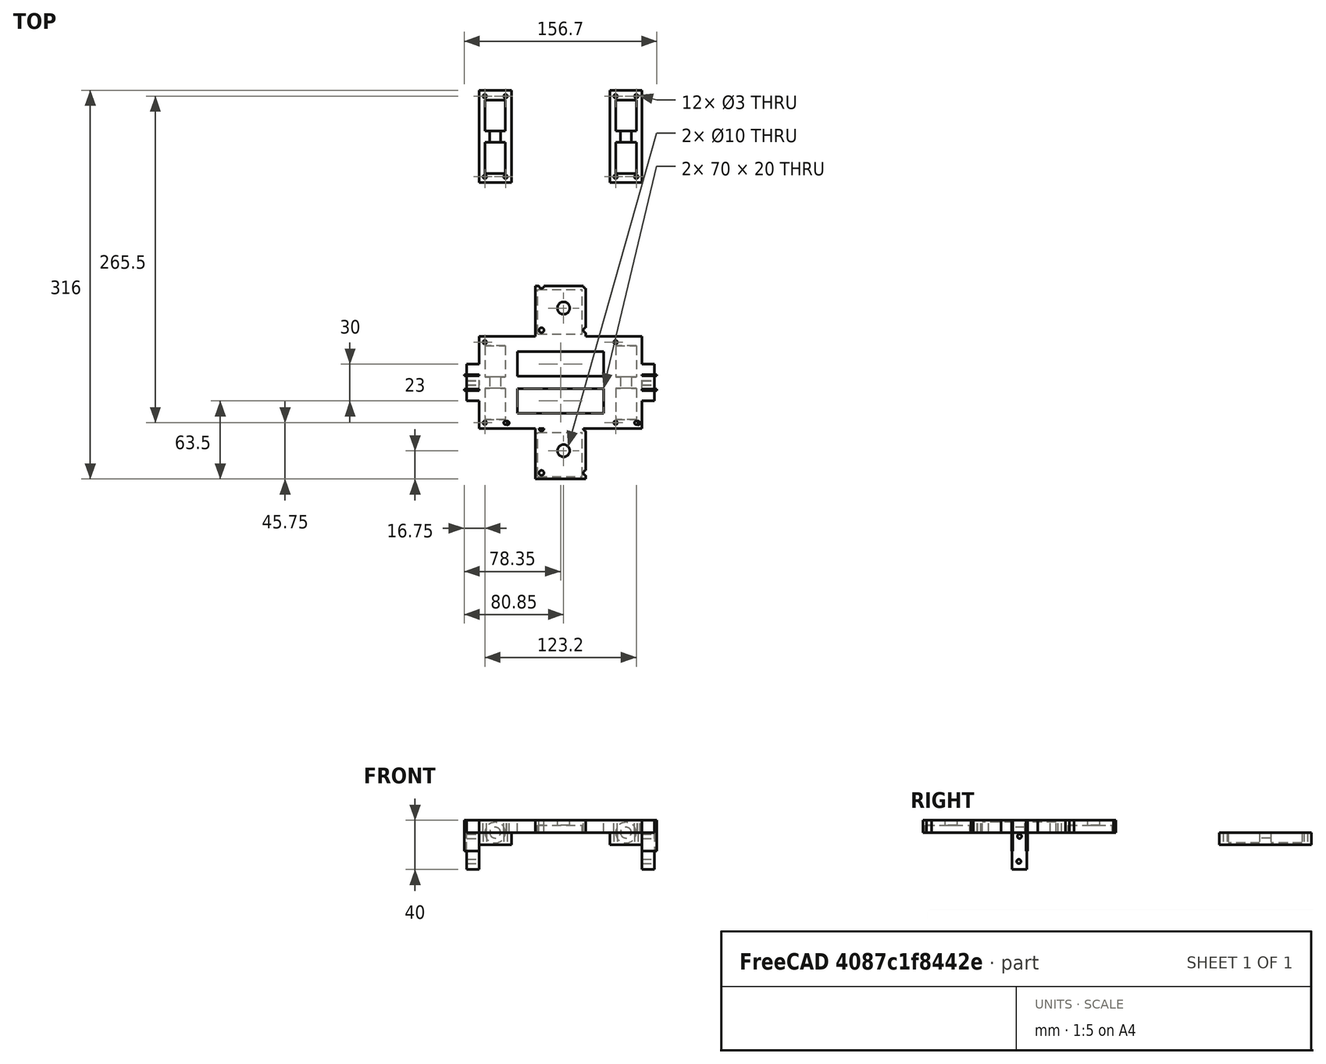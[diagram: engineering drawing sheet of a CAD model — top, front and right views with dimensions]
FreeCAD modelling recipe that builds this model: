
FCSTD DOCUMENT  (FreeCAD 0.16R6712 (Git))
Label: 1.2
License: All rights reserved
LicenseURL: http://en.wikipedia.org/wiki/All_rights_reserved
objects: Part::Cut×24, Part::Cylinder×21, Part::Box×14, Part::Fuse×5, Part::FeaturePython×4, Part::MultiFuse×4
note: 72 computed .brp shape members not serialized (recipe doc carries the construction recipe); baked Part::Feature solids carry a one-line shape summary decoded from their .brp

FEATURE [Part::Box] Box  label="Cubo"
  Height = 10
  Length = 26.35
  Width = 75
FEATURE [Part::Cylinder] Cylinder  label="Cilindro"
  Angle = 360
  Height = 10
  Placement = pos=(4.75,4.75,0) rot=(0,0,1;0rad)
  Radius = 1.5
FEATURE [Part::Cylinder] Cylinder002  label="Cilindro002"
  Angle = 360
  Height = 10
  Placement = pos=(4.75,70.25,0) rot=(0,0,1;0rad)
  Radius = 1.5
FEATURE [Part::Cylinder] Cylinder003  label="Cilindro003"
  Angle = 360
  Height = 10
  Placement = pos=(23.1425,4.56262,6.40077e-06) rot=(0,0,1;0rad)
  Radius = 1.5
FEATURE [Part::Cut] Cut
  Base = -> Box
  Tool = -> Cylinder
FEATURE [Part::Cut] Cut001
  Base = -> Cut
  Tool = -> Cylinder002
FEATURE [Part::Cut] Cut002
  Base = -> Cut001
  Tool = -> Cylinder003
FEATURE [Part::Cylinder] Cylinder004  label="Cilindro004"
  Angle = 360
  Height = 25.35
  Placement = pos=(13.175,30,0) rot=(1,0,0;1.5708rad)
  Radius = 8.4
FEATURE [Part::Cylinder] Cylinder005  label="Cilindro005"
  Angle = 360
  Height = 25.35
  Placement = pos=(13.175,64.5,0) rot=(1,0,0;1.5708rad)
  Radius = 8.4
FEATURE [Part::Cylinder] Cylinder006  label="Cilindro006"
  Angle = 360
  Height = 9.5
  Placement = pos=(13.175,39.5,0) rot=(1,0,0;1.5708rad)
  Radius = 4.4
FEATURE [Part::Fuse] Fusion
  Base = -> Cylinder004
  Tool = -> Cylinder005
FEATURE [Part::Fuse] Fusion001
  Base = -> Fusion
  Placement = pos=(0,2.75,0) rot=(0,0,1;0rad)
  Tool = -> Cylinder006
FEATURE [Part::Cylinder] Cylinder001  label="Cilindro001"
  Angle = 360
  Height = 10
  Placement = pos=(21.6,4.75,0) rot=(0,0,1;0rad)
  Radius = 1.5
FEATURE [Part::Cut] Cut004
  Base = -> Cut002
  Tool = -> Cylinder001
FEATURE [Part::Cut] Cut003
  Base = -> Cut002
  Tool = -> Cylinder001
FEATURE [Part::Fuse] Fusion002
  Base = -> Cut004
  Tool = -> Cut003
FEATURE [Part::Cut] Cut005
  Base = -> Fusion002
  Tool = -> Fusion001
FEATURE [Part::Cut] Cut006
  Base = -> Cut005
  Tool = -> Cylinder001
FEATURE [Part::FeaturePython] Array  label="Carrileras"  # Draft array (typed FeaturePython)
  Angle = 360
  ArrayType = 0
  Axis = (0,0,1)
  Base = -> Cut006
  Center = (0,0,0)
  Fuse = false
  IntervalAxis = (0,0,0)
  IntervalX = (106.35,0,0)
  IntervalY = (0,1,0)
  IntervalZ = (0,0,0)
  NumberPolar = 1
  NumberX = 2
  NumberY = 1
  NumberZ = 1
FEATURE [Part::Box] Box001  label="Centro"
  Height = 10
  Length = 80
  Placement = pos=(26.35,0,0) rot=(0,0,1;0rad)
  Width = 75
FEATURE [Part::Box] Box002  label="Lucernario"
  Height = 10
  Length = 70
  Placement = pos=(31.35,12.5,0) rot=(0,0,1;0rad)
  Width = 20
FEATURE [Part::Box] Box003  label="Lucernario2"
  Height = 10
  Length = 70
  Placement = pos=(31.35,42.5,0) rot=(0,0,1;0rad)
  Width = 20
FEATURE [Part::Cut] Cut007
  Base = -> Box001
  Tool = -> Box002
FEATURE [Part::Cut] Cut008  label="Centro1"
  Base = -> Cut007
  Tool = -> Box003
FEATURE [Part::Box] Box006  label="Guia1"
  Height = 10
  Length = 10
  Placement = pos=(-10,22.5,0) rot=(0,0,1;0rad)
  Width = 30
FEATURE [Part::Box] Box007  label="Guia2"
  Height = 10
  Length = 10
  Placement = pos=(132.7,22.5,0) rot=(0,0,1;0rad)
  Width = 30
FEATURE [Part::Fuse] Fusion005
  Base = -> Array
  Tool = -> Box006
FEATURE [Part::MultiFuse] Fusion006  label="Carrileras y guias"
  Shapes = -> [Fusion005,Box007]
FEATURE [Part::Box] Box010  label="Cubo003"
  Height = 10
  Length = 26.35
  Width = 75
FEATURE [Part::Cylinder] Cylinder007  label="Cilindro007"
  Angle = 360
  Height = 25.35
  Placement = pos=(13.175,67.25,0) rot=(1,0,0;1.5708rad)
  Radius = 8.4
FEATURE [Part::Cut] Cut011
  Base = -> Box010
  Tool = -> Cylinder007
FEATURE [Part::Cylinder] Cylinder008  label="Cilindro008"
  Angle = 360
  Height = 9.5
  Placement = pos=(13.175,42.25,0) rot=(1,0,0;1.5708rad)
  Radius = 4.4
FEATURE [Part::Cut] Cut012
  Base = -> Cut011
  Tool = -> Cylinder008
FEATURE [Part::Cylinder] Cylinder009  label="Cilindro009"
  Angle = 360
  Height = 25.35
  Placement = pos=(13.175,32.75,0) rot=(1,0,0;1.5708rad)
  Radius = 8.4
FEATURE [Part::Cut] Cut013
  Base = -> Cut012
  Tool = -> Cylinder009
FEATURE [Part::Cylinder] Cylinder010  label="Cilindro010"
  Angle = 360
  Height = 10
  Placement = pos=(21.6,4.75,0) rot=(0,0,1;0rad)
  Radius = 1.5
FEATURE [Part::Cylinder] Cylinder011  label="Cilindro011"
  Angle = 360
  Height = 10
  Placement = pos=(4.75,4.75,0) rot=(0,0,1;0rad)
  Radius = 1.5
FEATURE [Part::Cut] Cut014
  Base = -> Cut013
  Tool = -> Cylinder010
FEATURE [Part::Cut] Cut015
  Base = -> Cut014
  Tool = -> Cylinder011
FEATURE [Part::Cylinder] Cylinder012  label="Cilindro012"
  Angle = 360
  Height = 10
  Placement = pos=(4.75,70.25,0) rot=(0,0,1;0rad)
  Radius = 1.5
FEATURE [Part::Cylinder] Cylinder013  label="Cilindro013"
  Angle = 360
  Height = 10
  Placement = pos=(21.6,70.25,0) rot=(0,0,1;0rad)
  Radius = 1.5
FEATURE [Part::Cut] Cut016
  Base = -> Cut015
  Tool = -> Cylinder012
FEATURE [Part::Cut] Cut017
  Base = -> Cut016
  Placement = pos=(0,0,0) rot=(0,1,0;3.14159rad)
  Tool = -> Cylinder013
FEATURE [Part::FeaturePython] Array001  label="Cierres"  # Draft array (typed FeaturePython)
  Angle = 360
  ArrayType = 0
  Axis = (0,0,1)
  Base = -> Cut017
  Center = (0,0,0)
  Fuse = false
  IntervalAxis = (0,0,0)
  IntervalX = (106.35,0,0)
  IntervalY = (0,1,0)
  IntervalZ = (0,0,0)
  NumberPolar = 1
  NumberX = 2
  NumberY = 1
  NumberZ = 1
  Placement = pos=(26.35,200,0) rot=(0,0,1;0rad)
FEATURE [Part::Box] Box011  label="Cubo004"
  Height = 10
  Length = 41
  Width = 41
FEATURE [Part::Cylinder] Cylinder014  label="Cilindro014"
  Angle = 360
  Height = 10
  Placement = pos=(5,5,0) rot=(0,0,1;0rad)
  Radius = 2
FEATURE [Part::Cylinder] Cylinder015  label="Cilindro015"
  Angle = 360
  Height = 10
  Placement = pos=(5,41,0) rot=(0,0,1;0rad)
  Radius = 2
FEATURE [Part::Cylinder] Cylinder016  label="Cilindro016"
  Angle = 360
  Height = 10
  Placement = pos=(41,5,0) rot=(0,0,1;0rad)
  Radius = 2
FEATURE [Part::Cylinder] Cylinder017  label="Cilindro017"
  Angle = 360
  Height = 10
  Placement = pos=(41,41,0) rot=(0,0,1;0rad)
  Radius = 2
FEATURE [Part::Cylinder] Cylinder018  label="Cilindro018"
  Angle = 360
  Height = 10
  Placement = pos=(23,23,0) rot=(0,0,1;0rad)
  Radius = 5
FEATURE [Part::Cut] Cut018
  Base = -> Box011
  Tool = -> Cylinder015
FEATURE [Part::Cut] Cut019
  Base = -> Cut018
  Tool = -> Cylinder014
FEATURE [Part::Cut] Cut020
  Base = -> Cut019
  Tool = -> Cylinder016
FEATURE [Part::Cut] Cut021
  Base = -> Cut020
  Tool = -> Cylinder017
FEATURE [Part::Cut] Cut022
  Base = -> Cut021
  Tool = -> Cylinder018
FEATURE [Part::Box] Box012  label="Cubo005"
  Height = 6
  Length = 36
  Placement = pos=(2,2,0) rot=(0,0,1;0rad)
  Width = 36
FEATURE [Part::Cut] Cut023
  Base = -> Cut022
  Placement = pos=(43.35,-46,0) rot=(0,0,1;0rad)
  Tool = -> Box012
FEATURE [Part::FeaturePython] Array002  # Draft array (typed FeaturePython)
  Angle = 360
  ArrayType = 0
  Axis = (0,0,1)
  Base = -> Cut023
  Center = (0,0,0)
  Fuse = false
  IntervalAxis = (0,0,0)
  IntervalX = (1,0,0)
  IntervalY = (0,116,0)
  IntervalZ = (0,0,0)
  NumberPolar = 1
  NumberX = 1
  NumberY = 2
  NumberZ = 1
  Placement = pos=(2.5,5,0) rot=(0,0,1;0rad)
FEATURE [Part::Fuse] Fusion007
  Base = -> Cut008
  Tool = -> Fusion006
FEATURE [Part::MultiFuse] Fusion008
  Shapes = -> [Fusion007,Array002]
FEATURE [Part::Box] Box014  label="Cubo007"
  Height = 25
  Length = 12
  Placement = pos=(132.7,31,-15) rot=(0,0,1;0rad)
  Width = 1
FEATURE [Part::Box] Box015  label="Cubo008"
  Height = 25
  Length = 12
  Placement = pos=(132.7,43,-15) rot=(0,0,1;0rad)
  Width = 1
FEATURE [Part::Box] Box016  label="Cubo009"
  Height = 30
  Length = 10
  Placement = pos=(-10,31.5,-30) rot=(0,0,1;0rad)
  Width = 12
FEATURE [Part::Box] Box017  label="Cubo010"
  Height = 25
  Length = 12
  Placement = pos=(-12,31,-15) rot=(0,0,1;0rad)
  Width = 1
FEATURE [Part::Box] Box018  label="Cubo011"
  Height = 25
  Length = 12
  Placement = pos=(-12,43,-15) rot=(0,0,1;0rad)
  Width = 1
FEATURE [Part::Cylinder] Cylinder019  label="Cilindro019"
  Angle = 360
  Height = 10
  Placement = pos=(-10,37.5,-3) rot=(0,1,0;1.5708rad)
  Radius = 1.75
FEATURE [Part::Cylinder] Cylinder020  label="Cilindro020"
  Angle = 360
  Height = 10
  Placement = pos=(-10,37,-23.5) rot=(0,1,0;1.5708rad)
  Radius = 1.75
FEATURE [Part::Cut] Cut024
  Base = -> Box016
  Tool = -> Cylinder020
FEATURE [Part::Cut] Cut025
  Base = -> Cut024
  Tool = -> Cylinder019
FEATURE [Part::FeaturePython] Array003  # Draft array (typed FeaturePython)
  Angle = 360
  ArrayType = 0
  Axis = (0,0,1)
  Base = -> Cut025
  Center = (0,0,0)
  Fuse = false
  IntervalAxis = (0,0,0)
  IntervalX = (142.7,0,0)
  IntervalY = (0,1,0)
  IntervalZ = (0,0,0)
  NumberPolar = 1
  NumberX = 2
  NumberY = 1
  NumberZ = 1
FEATURE [Part::MultiFuse] Fusion009
  Shapes = -> [Box015,Box014,Array003]
FEATURE [Part::MultiFuse] Fusion010
  Shapes = -> [Fusion009,Box018,Box017]
